# Revit family: 1421xxx Cambria 580
name_source: partatom
category: Lighting Fixtures
revit_build: Autodesk Revit 2018 (Build: 20170223_1515(x64)
units: mm (PartAtom-declared; Revit-internal decimal feet)

## family parameters
Always vertical = Yes
Cut with Voids When Loaded = No
Host = Ceiling
Light Source = No
OmniClass Number = 23.80.70.11
OmniClass Title = Luminaries for Internal Lighting
Part Type = Normal
Room Calculation Point = No
Round Connector Dimension = Use Diameter
Shared = No

## types (2) — shared parameters
Manufacturer URL - Europe and Rest of World = www.astrolighting.com
Manufacturer URL - North America = us.astrolighting.com

## per-type parameters (varying)
| type | Dimmable | Dimming Method | Driver Required | Electrical Class | Lamp | Light Source Fixed | Location / IP Rating | Main Finish | Main Material | Power (Watts) | Product CCT | Product CRI | Product Dimensions (MM) | Product Location | Product Name | Product SKU | Product Weight (KG) |
| CE |  |  |  |  |  |  |  |  |  |  | 2700K / 3000K | 80 / 90 |  |  |  | 1234567 | 0 mm  [stored 0 ft] |
| ETL | Yes | Lamp Dependant | No | Class  I | 3 x 12W Max - LED GLS E27/ES | Yes | IP20 | Cambria 580 | Fabric Shade | 12W | Lamp Dependent | Lamp Dependent | 137 x 380 | Interior | Cambria 580 | 1421xxx | 1 mm  [stored 0.00328084 ft] |

note: [stored X ft] marks values corroborated as IEEE doubles in the binary element streams (Revit-internal decimal feet)

## geometry (parser evidence)
native form markers: Sweep x2
no freeform markers — native parametric forms only
